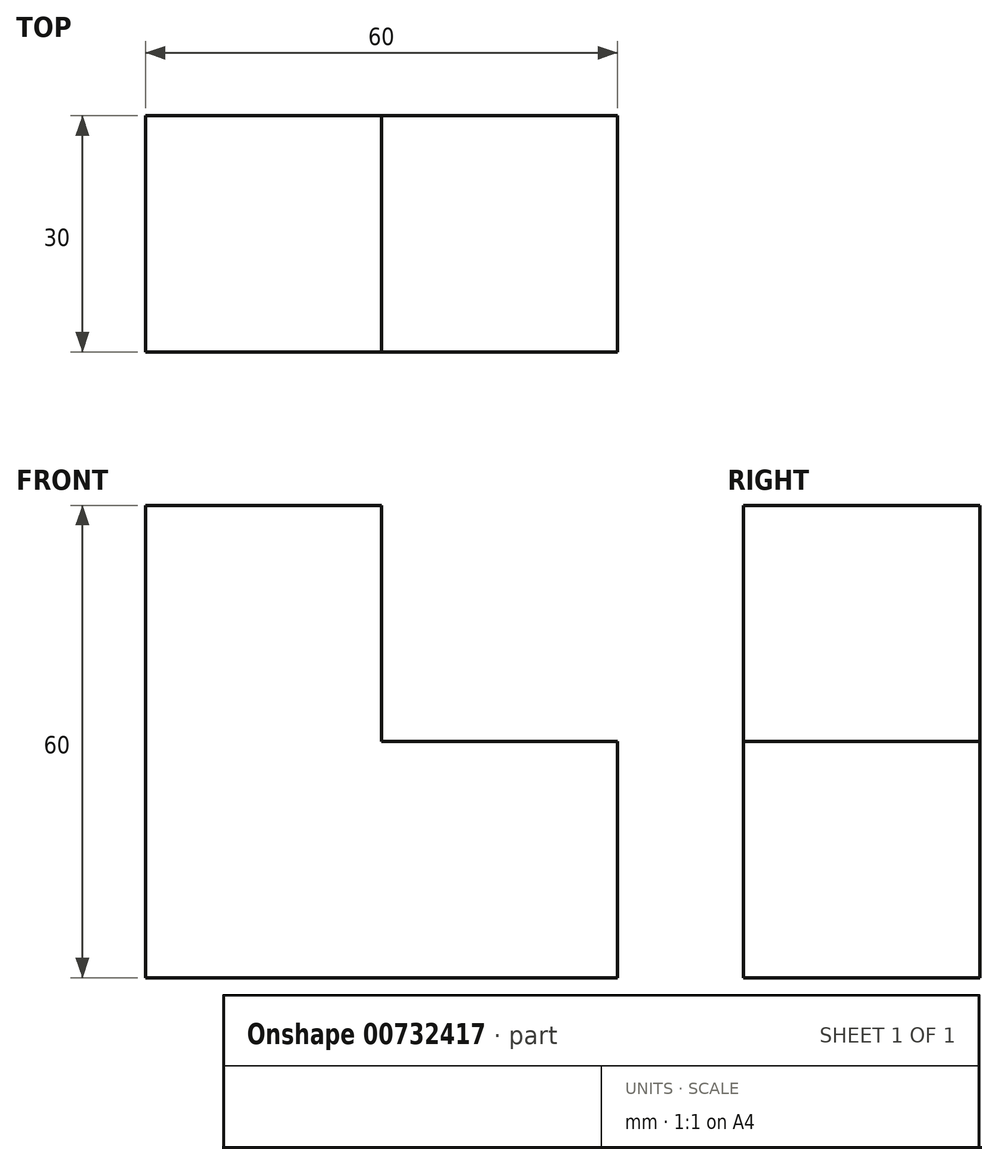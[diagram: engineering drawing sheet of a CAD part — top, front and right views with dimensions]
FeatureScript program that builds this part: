
annotation { "Feature Type Name" : "Feature", "Feature Type Description" : "" }
export const myFeature = defineFeature(function(context is Context, id is Id, definition is map)
    precondition{}
    {
        {
            var Q0;
            Q0=qCreatedBy(makeId("Front.planeOp"),FACE);
            var sketch = newSketch(context, id + "F0", { "sketchPlane" : qUnion([Q0])});
            skLineSegment(sketch, "E0", {"start": v(-60, 60) * mm, "end": v(-60, 0) * mm});
            skLineSegment(sketch, "E1", {"start": v(-60, 0) * mm, "end": v(0, 0) * mm});
            skLineSegment(sketch, "E2", {"start": v(0, 0) * mm, "end": v(0, 30) * mm});
            skLineSegment(sketch, "E3", {"start": v(0, 30) * mm, "end": v(-60, 30) * mm});
            skLineSegment(sketch, "E4", {"start": v(-60, 30) * mm, "end": v(-30, 30) * mm});
            skLineSegment(sketch, "E5", {"start": v(-30, 30) * mm, "end": v(-30, 60) * mm});
            skLineSegment(sketch, "E6", {"start": v(-30, 60) * mm, "end": v(-60, 60) * mm});
            skSolve(sketch);
        }
        {
            var Q0;
            {var subQ0=sQuery(id+"F0.wireOp",EDGE,"E5");var subQ7=sQuery(id+"F0.wireOp",EDGE,"E1");Q0=qUnion([makeQuery(id+"F0.imprint","IMPRINT",FACE,{"disambiguationData":[TD([[makeQuery(id+"F0.imprint","IMPRINT",EDGE,{"derivedFrom":subQ0}),1.0]])]}),makeQuery(id+"F0.imprint","IMPRINT",FACE,{"disambiguationData":[TD([[makeQuery(id+"F0.imprint","IMPRINT",EDGE,{"derivedFrom":subQ7}),1.0]])]})]);}
            extrude(context, id + "F1", {"entities" : qUnion([Q0]), "depth" : 30 * mm, "offsetDistance" : 25 * mm});
        }
    });
